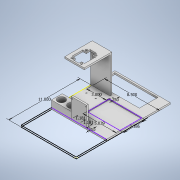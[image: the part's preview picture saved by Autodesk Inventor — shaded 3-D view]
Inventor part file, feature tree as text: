
AUTODESK INVENTOR PART (.ipt)
format: ipt  version: 2020 (Build 240168000, 168)  size: 246,272 bytes
history: native  units: in
note: dims shown in document units (in); Inventor stores cm internally (conversion verified against a paired STEP export)
features: extrude x11, sketch x9, hole x2
ambient origin geometry x8: Origin, YZ Plane, XZ Plane, XY Plane, X Axis, Y Axis, Z Axis, Center Point
bodies: Solid1 (feature_tree)
feature tree (22):
  sketch  "Sketch1"  dims[d0=8.5in d1=11.0in]
  extrude  "Extrusion1"  Depth=8.5in
  extrude  "Extrusion2"  Depth=0.25in
  extrude  "Extrusion3"  Depth=0.25in TaperAngle=0.0deg
  hole  "Hole1"  [1 undecoded]
  extrude  "Extrusion4"  Depth=0.375in
  sketch  "Sketch5"  dims[d11=0.375in d12=0.72in]
  extrude  "Extrusion5"  Depth=2.19in
  extrude  "Extrusion6"  Depth=0.625in
  extrude  "Extrusion7"  Depth=1.94in
  extrude  "Extrusion8"  Depth=4.0in TaperAngle=0.0deg
  extrude  "Extrusion9"  Depth=5.0394in
  hole  "Hole2"  [1 undecoded]
  extrude  "Extrusion10"  Depth=0.15in TaperAngle=0.0deg
  extrude  "Extrusion11"  Depth=1.0in TaperAngle=0.0deg
  sketch  "Sketch2"  dims[d2=3.0in d3=0.25in]
  sketch  "Sketch3"  dims[d4=6.0in d5=0.0in d6=0.25in d7=0.0in]
  sketch  "Sketch4"  dims[d8=0.25in d9=4.0in d10=0.0in]
  sketch  "Sketch6"  dims[d13=0.72in d14=2.19in]
  sketch  "Sketch7"  dims[d15=2.19in]
  sketch  "Sketch9"  dims[d16=0.177in d17=0.75in d18=0.313in d19=0.164in d20=0.5635in d21=1.0in d22=0.8108in d23=0.625in]
  sketch  "Sketch10"  dims[d24=0.5in d25=1.94in d26=4.0in d27=0.0in d28=5.0394in d29=3.3858in d30=0.15in d31=0.0in d32=1.0in d33=0.0in d34=0.75in d35=180.0deg d36=1.1417in d37=0.75in d38=0.0in d39=1.1417in d40=1.15in d41=0.0in d42=1.1811in d43=0.25in d44=1.1811in d45=3.0in d46=0.0in d47=3.0in d48=0.0in d49=1.0433in d50=0.25in d51=1.0433in d52=0.145in d53=0.38in d54=0.313in d55=0.164in d56=0.5635in d57=1.0in d58=0.8108in d59=3.5in d60=0.0in d61=0.25in d62=0.25in d63=6.625in d64=2.875in d65=0.25in d66=0.0in]
note: 2 required parameter values undecoded (feature->parameter linkage not recoverable at this tier; creation-order binding heuristic only, values carry confidence <= 0.55)
